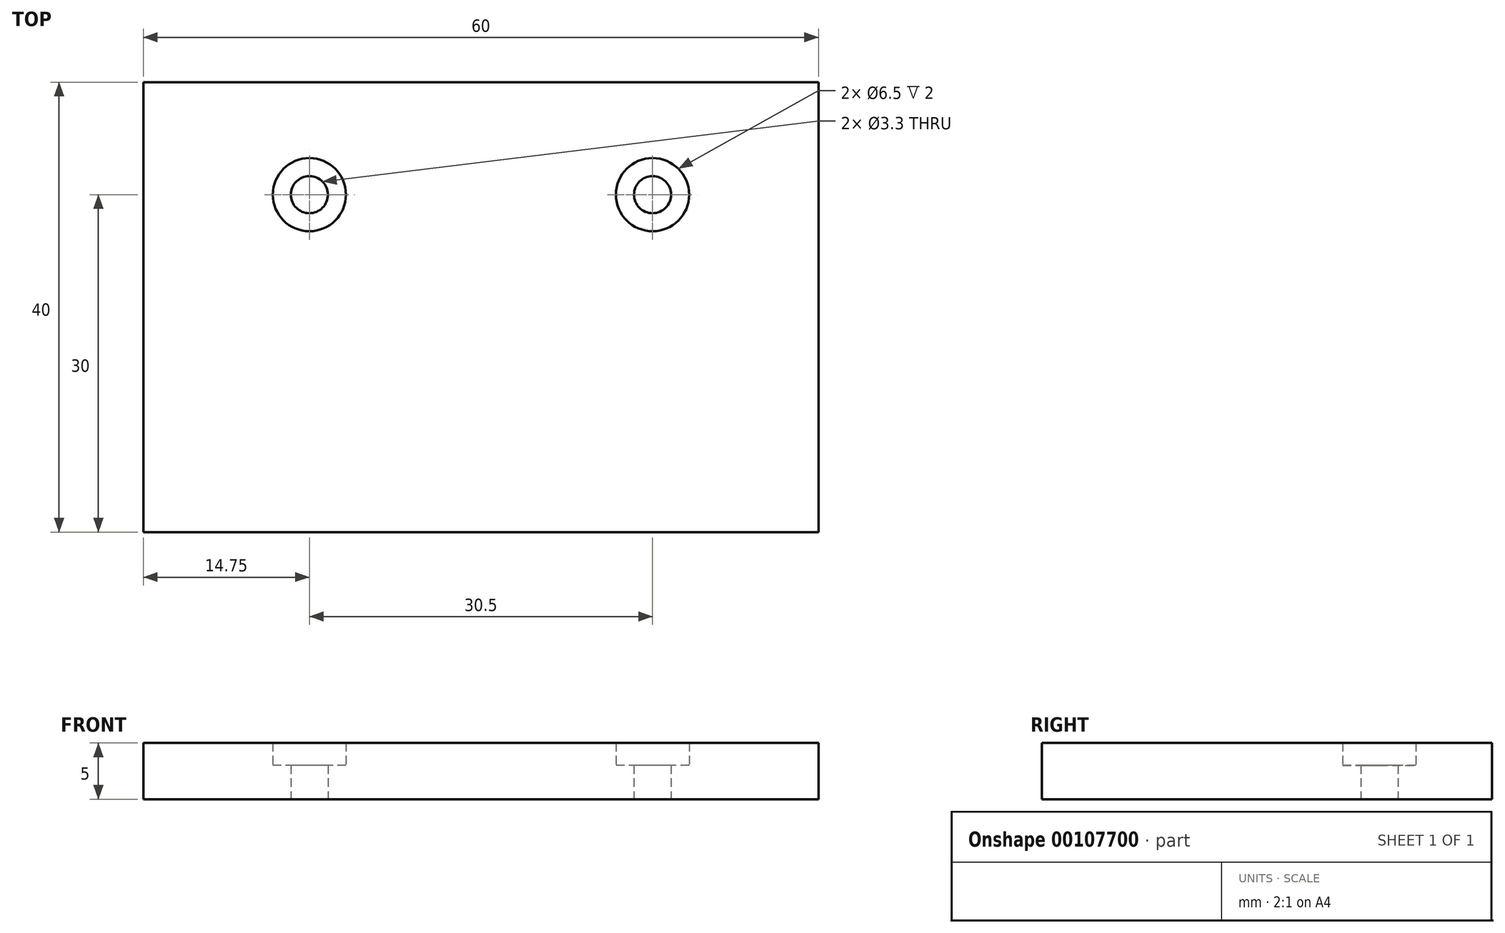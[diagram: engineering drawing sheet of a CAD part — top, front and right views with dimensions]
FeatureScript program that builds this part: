
annotation { "Feature Type Name" : "Feature", "Feature Type Description" : "" }
export const myFeature = defineFeature(function(context is Context, id is Id, definition is map)
    precondition{}
    {
        {
            var Q0;
            Q0=qCreatedBy(makeId("Top.planeOp"),FACE);
            var sketch = newSketch(context, id + "F0", { "sketchPlane" : qUnion([Q0])});
            skLineSegment(sketch, "E0.bottom", {"start": v(30, -20) * mm, "end": v(-30, -20) * mm});
            skLineSegment(sketch, "E0.top", {"start": v(30, 20) * mm, "end": v(-30, 20) * mm});
            skLineSegment(sketch, "E0.left", {"start": v(30, -20) * mm, "end": v(30, 20) * mm});
            skLineSegment(sketch, "E0.right", {"start": v(-30, -20) * mm, "end": v(-30, 20) * mm});
            skPoint(sketch, "E0.middle", {"position": v(0, 0) * mm});
            skLineSegment(sketch, "E1", {"start": v(-30, 10) * mm, "end": v(30, 10) * mm, "construction": true});
            skLineSegment(sketch, "E2", {"start": v(-15.25, 20) * mm, "end": v(-15.25, -20) * mm, "construction": true});
            skLineSegment(sketch, "E3", {"start": v(15.25, 20) * mm, "end": v(15.25, -20) * mm, "construction": true});
            skLineSegment(sketch, "E4", {"start": v(0, 20) * mm, "end": v(0, -20) * mm, "construction": true});
            skCircle(sketch, "E5", {"center": v(-15.25, 10) * mm, "radius": 1.65 * mm});
            skCircle(sketch, "E6", {"center": v(-15.25, 10) * mm, "radius": 3.25 * mm});
            skCircle(sketch, "E7", {"center": v(15.25, 10) * mm, "radius": 1.65 * mm});
            skCircle(sketch, "E8", {"center": v(15.25, 10) * mm, "radius": 3.25 * mm});
            skSolve(sketch);
        }
        {
            var Q0;
            Q0=makeQuery(id+"F0.imprint","IMPRINT",FACE,{"disambiguationData":[TD([[makeQuery(id+"F0.imprint","IMPRINT",EDGE,{"derivedFrom":sQuery(id+"F0.wireOp",EDGE,"E0.bottom")}),-1.0]])]});
            extrude(context, id + "F1", {"entities" : qUnion([Q0]), "depth" : 5 * mm});
        }
        {
            var Q0;
            Q0=makeQuery(id+"F0.imprint","IMPRINT",FACE,{"disambiguationData":[TD([[makeQuery(id+"F0.imprint","IMPRINT",EDGE,{"derivedFrom":sQuery(id+"F0.wireOp",EDGE,"E7")}),-1.0]])]});
            var Q1;
            Q1=makeQuery(id+"F0.imprint","IMPRINT",FACE,{"disambiguationData":[TD([[makeQuery(id+"F0.imprint","IMPRINT",EDGE,{"derivedFrom":sQuery(id+"F0.wireOp",EDGE,"E5")}),-1.0]])]});
            extrude(context, id + "F2", {"entities" : qUnion([Q0, Q1]), "operationType" : NewBodyOperationType.ADD, "depth" : 3 * mm});
        }
    });
